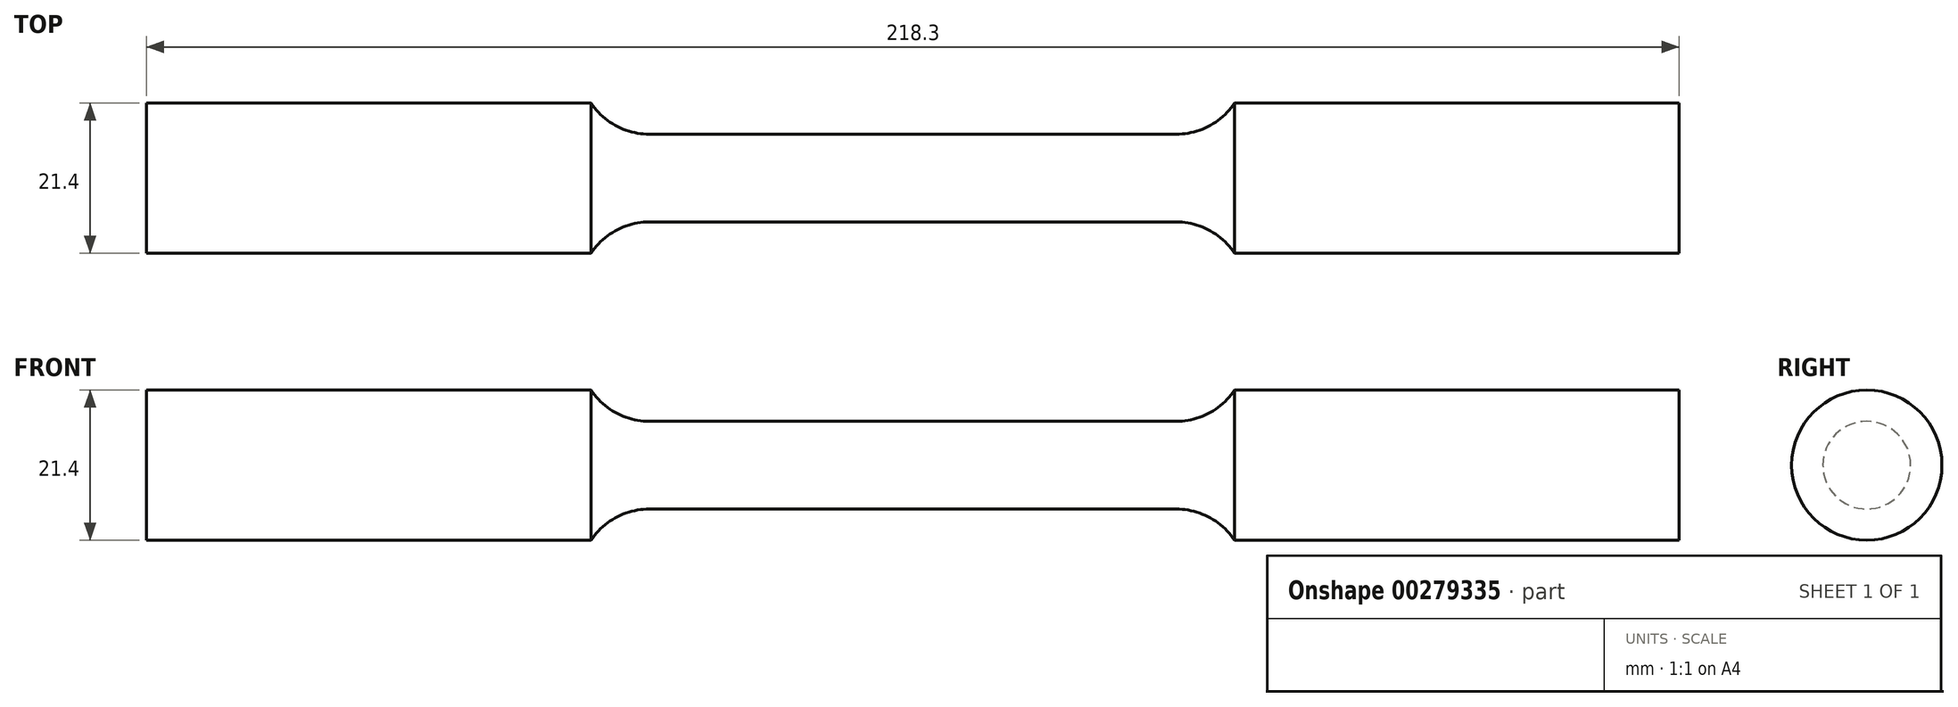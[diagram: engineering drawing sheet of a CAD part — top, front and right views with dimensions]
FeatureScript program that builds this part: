
annotation { "Feature Type Name" : "Feature", "Feature Type Description" : "" }
export const myFeature = defineFeature(function(context is Context, id is Id, definition is map)
    precondition{}
    {
        {
            var Q0;
            Q0=qCreatedBy(makeId("Front.planeOp"),FACE);
            var sketch = newSketch(context, id + "F0", { "sketchPlane" : qUnion([Q0])});
            skLineSegment(sketch, "E0", {"start": v(0, 6.25) * mm, "end": v(37.5, 6.25) * mm});
            skArc(sketch, "E1", {"start": v(37.5, 6.25) * mm, "mid": v(42.22, 7.43) * mm, "end": v(45.82, 10.7) * mm});
            skLineSegment(sketch, "E2", {"start": v(45.82, 10.7) * mm, "end": v(109.15, 10.7) * mm});
            skLineSegment(sketch, "E3", {"start": v(109.15, 10.7) * mm, "end": v(109.15, 0) * mm});
            skLineSegment(sketch, "E4.MirrorCS", {"start": v(0, 6.25) * mm, "end": v(-37.5, 6.25) * mm});
            skLineSegment(sketch, "E5.MirrorCS", {"start": v(-109.15, 10.7) * mm, "end": v(-109.15, 0) * mm});
            skLineSegment(sketch, "E6.MirrorCS", {"start": v(-45.82, 10.7) * mm, "end": v(-109.15, 10.7) * mm});
            skArc(sketch, "E7.MirrorCS", {"start": v(-37.5, 6.25) * mm, "mid": v(-42.22, 7.43) * mm, "end": v(-45.82, 10.7) * mm});
            skLineSegment(sketch, "E8", {"start": v(-109.15, 0) * mm, "end": v(109.15, 0) * mm});
            skSolve(sketch);
        }
        {
            var Q0;
            Q0 = qSketchRegion(id + "F0", true);
            var Q1;
            Q1=sQuery(id+"F0.wireOp",EDGE,"E8");
            revolve(context, id + "F1", {"entities" : qUnion([Q0]), "axis" : qUnion([Q1]), "revolveType" : RevolveType.FULL});
        }
    });
